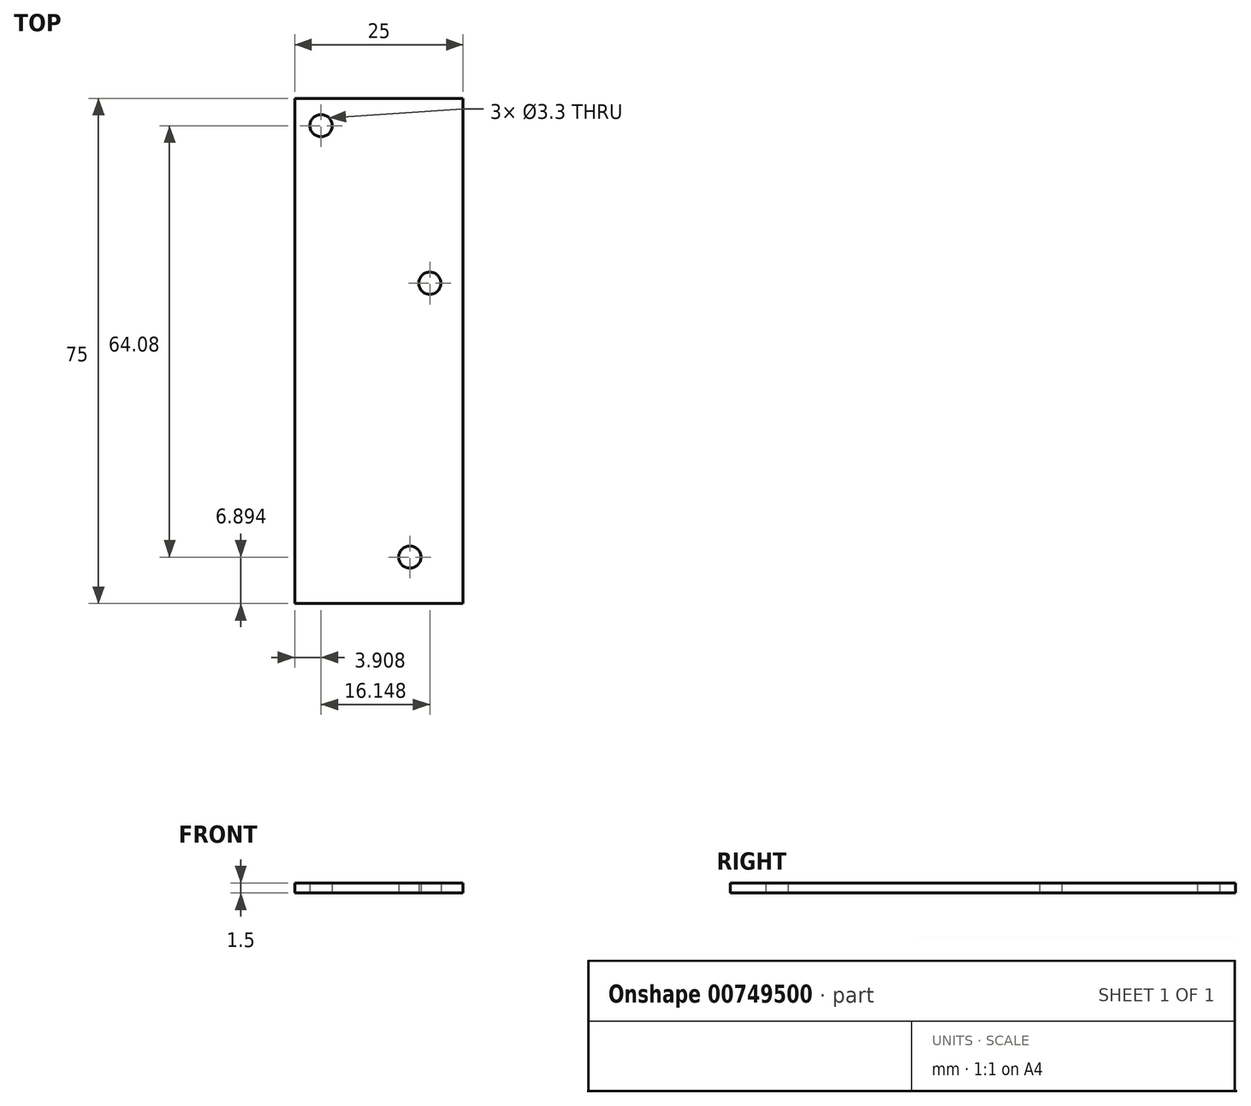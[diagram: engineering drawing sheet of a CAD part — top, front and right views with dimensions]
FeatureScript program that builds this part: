
annotation { "Feature Type Name" : "Feature", "Feature Type Description" : "" }
export const myFeature = defineFeature(function(context is Context, id is Id, definition is map)
    precondition{}
    {
        {
            var Q0;
            Q0=qCreatedBy(makeId("Top.planeOp"),FACE);
            var sketch = newSketch(context, id + "F0", { "sketchPlane" : qUnion([Q0])});
            skLineSegment(sketch, "E0.bottom", {"start": v(0, 0) * mm, "end": v(25, 0) * mm});
            skLineSegment(sketch, "E0.top", {"start": v(0, 75) * mm, "end": v(25, 75) * mm});
            skLineSegment(sketch, "E0.left", {"start": v(0, 0) * mm, "end": v(0, 75) * mm});
            skLineSegment(sketch, "E0.right", {"start": v(25, 0) * mm, "end": v(25, 75) * mm});
            skCircle(sketch, "E1", {"center": v(17.1, 6.9) * mm, "radius": 1.65 * mm});
            skCircle(sketch, "E2", {"center": v(3.9, 70.97) * mm, "radius": 1.65 * mm});
            skCircle(sketch, "E3", {"center": v(20.06, 47.57) * mm, "radius": 1.65 * mm});
            skSolve(sketch);
        }
        {
            var Q0;
            Q0=makeQuery(id+"F0.imprint","IMPRINT",FACE,{"disambiguationData":[TD([[makeQuery(id+"F0.imprint","IMPRINT",EDGE,{"derivedFrom":sQuery(id+"F0.wireOp",EDGE,"E0.bottom")}),1.0]])]});
            extrude(context, id + "F1", {"entities" : qUnion([Q0]), "depth" : 1.5 * mm, "offsetDistance" : 25 * mm});
        }
    });
